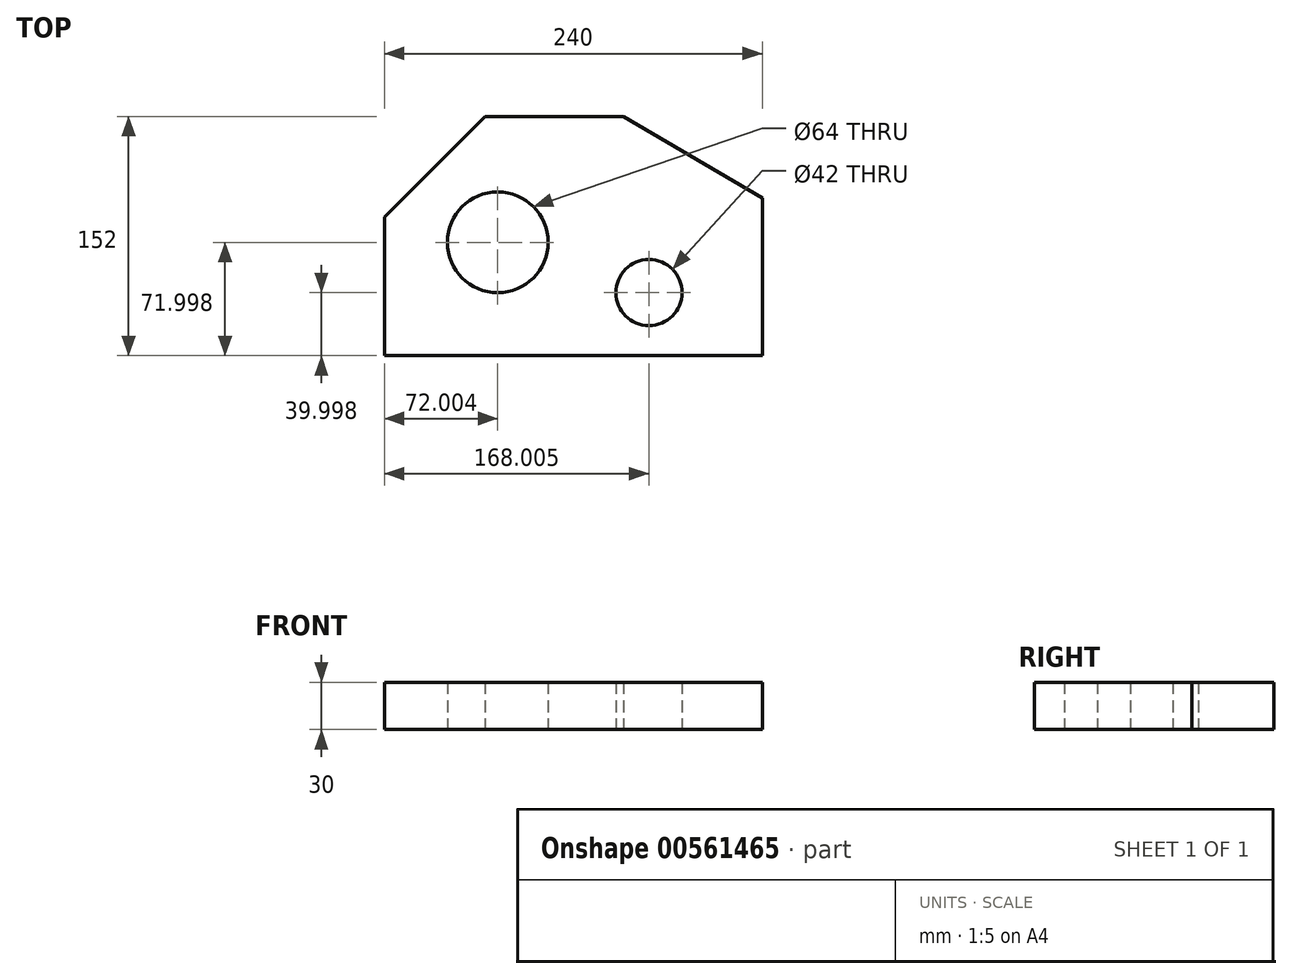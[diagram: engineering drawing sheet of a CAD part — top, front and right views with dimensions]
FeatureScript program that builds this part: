
annotation { "Feature Type Name" : "Feature", "Feature Type Description" : "" }
export const myFeature = defineFeature(function(context is Context, id is Id, definition is map)
    precondition{}
    {
        {
            var Q0;
            Q0=qCreatedBy(makeId("Top.planeOp"),FACE);
            var sketch = newSketch(context, id + "F0", { "sketchPlane" : qUnion([Q0])});
            skLineSegment(sketch, "E0", {"start": v(-45.19, -32.52) * mm, "end": v(194.81, -32.52) * mm});
            skLineSegment(sketch, "E1", {"start": v(194.81, -32.52) * mm, "end": v(194.81, 67.48) * mm});
            skLineSegment(sketch, "E2", {"start": v(-45.19, -32.52) * mm, "end": v(-45.19, 55.48) * mm});
            skLineSegment(sketch, "E3", {"start": v(-45.19, 55.48) * mm, "end": v(18.81, 119.48) * mm});
            skLineSegment(sketch, "E4", {"start": v(18.81, 119.48) * mm, "end": v(106.81, 119.48) * mm});
            skLineSegment(sketch, "E5", {"start": v(106.81, 119.48) * mm, "end": v(194.81, 67.48) * mm});
            skCircle(sketch, "E6", {"center": v(26.81, 39.48) * mm, "radius": 32 * mm});
            skCircle(sketch, "E7", {"center": v(122.81, 7.48) * mm, "radius": 21 * mm});
            skSolve(sketch);
        }
        {
            var Q0;
            Q0=makeQuery(id+"F0.imprint","IMPRINT",FACE,{"disambiguationData":[TD([[makeQuery(id+"F0.imprint","IMPRINT",EDGE,{"derivedFrom":sQuery(id+"F0.wireOp",EDGE,"E0")}),1.0]])]});
            extrude(context, id + "F1", {"entities" : qUnion([Q0]), "depth" : 30 * mm, "offsetDistance" : 25 * mm});
        }
    });
